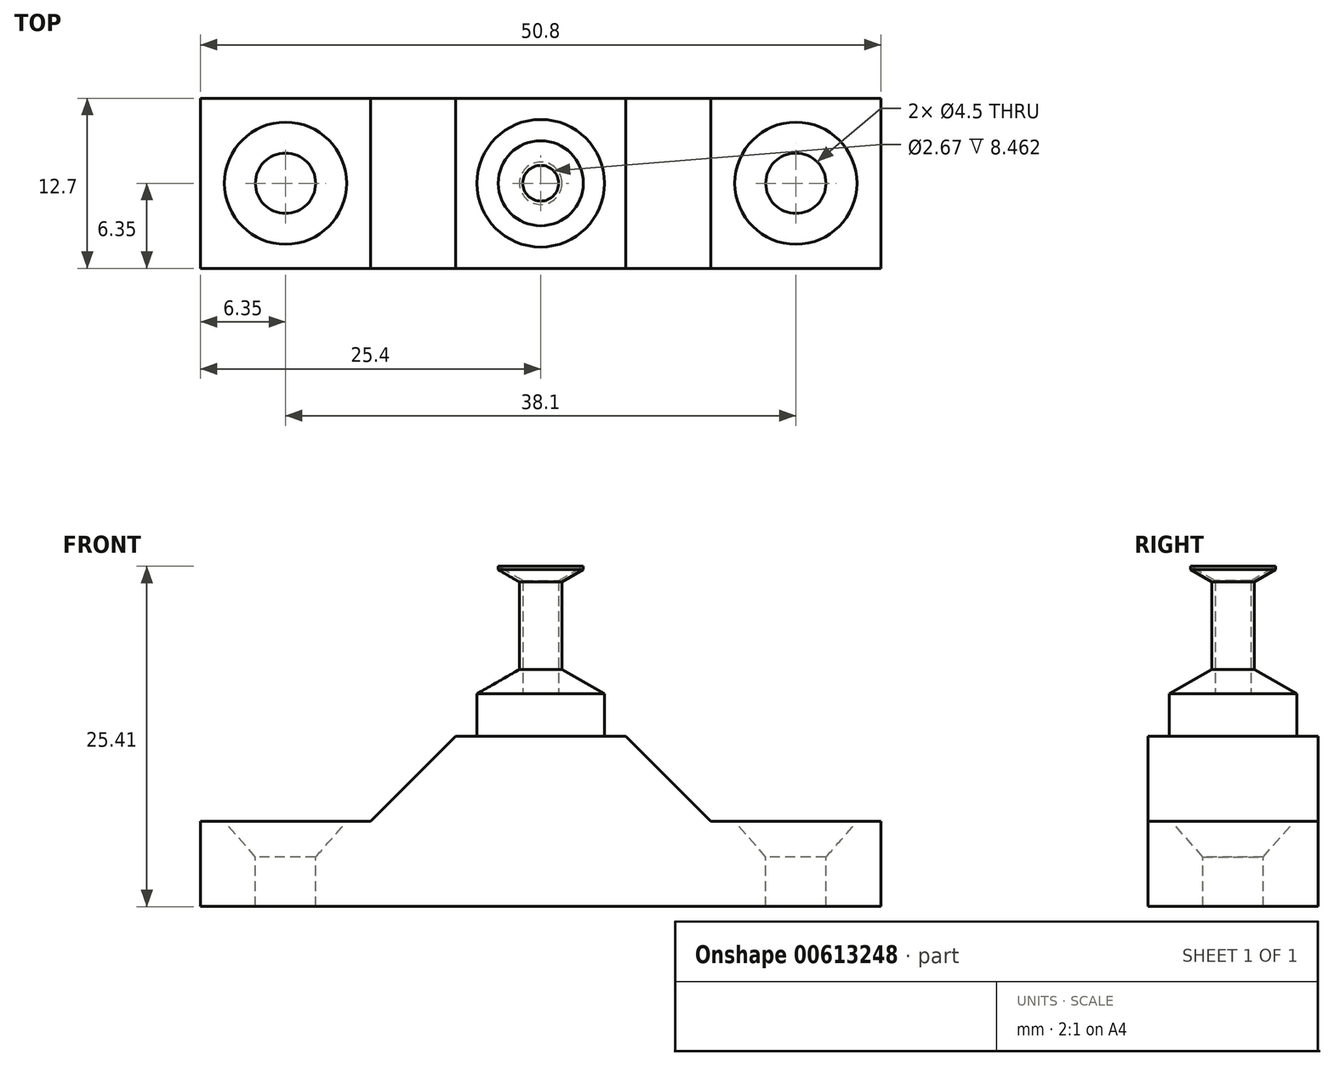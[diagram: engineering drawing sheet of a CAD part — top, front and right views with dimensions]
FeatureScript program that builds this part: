
annotation { "Feature Type Name" : "Feature", "Feature Type Description" : "" }
export const myFeature = defineFeature(function(context is Context, id is Id, definition is map)
    precondition{}
    {
        {
            var Q0;
            Q0=qCreatedBy(makeId("Front.planeOp"),FACE);
            var sketch = newSketch(context, id + "F0", { "sketchPlane" : qUnion([Q0])});
            skLineSegment(sketch, "E0.bottom", {"start": v(25.4, 3.18) * mm, "end": v(12.7, 3.18) * mm});
            skLineSegment(sketch, "E0.top", {"start": v(25.4, -3.18) * mm, "end": v(-25.4, -3.18) * mm});
            skLineSegment(sketch, "E0.left", {"start": v(25.4, 3.18) * mm, "end": v(25.4, -3.18) * mm});
            skLineSegment(sketch, "E0.right", {"start": v(-25.4, 3.18) * mm, "end": v(-25.4, -3.18) * mm});
            skPoint(sketch, "E0.middle", {"position": v(0, 0) * mm});
            skLineSegment(sketch, "E1", {"start": v(-12.7, 3.18) * mm, "end": v(-6.35, 9.53) * mm});
            skLineSegment(sketch, "E2", {"start": v(-6.35, 9.53) * mm, "end": v(6.35, 9.53) * mm});
            skLineSegment(sketch, "E3", {"start": v(6.35, 9.53) * mm, "end": v(12.7, 3.18) * mm});
            skLineSegment(sketch, "E4.trimOffspring", {"start": v(-12.7, 3.18) * mm, "end": v(-25.4, 3.18) * mm});
            skSolve(sketch);
        }
        {
            var Q0;
            Q0 = qSketchRegion(id + "F0", true);
            extrude(context, id + "F1", {"entities" : qUnion([Q0]), "endBound" : BoundingType.SYMMETRIC, "depth" : 12.7 * mm, "offsetDistance" : 25.4 * mm});
        }
        {
            var Q0;
            Q0=makeQuery(id+"F1.opExtrude","SWEPT_FACE",FACE,{"disambiguationData":[OSD([sQuery(id+"F0.wireOp",EDGE,"E4.trimOffspring")])]});
            var sketch = newSketch(context, id + "F2", { "sketchPlane" : qUnion([Q0])});
            skPoint(sketch, "E5", {"position": v(-19.05, 0) * mm});
            skPoint(sketch, "E6", {"position": v(19.05, 0) * mm});
            skSolve(sketch);
        }
        {
            var Q0;
            Q0=sQuery(id+"F2.wireOp",VERTEX,"E5");
            var Q1;
            Q1=sQuery(id+"F2.wireOp",VERTEX,"E6");
            var Q2;
            Q2=makeQuery(id+"F1.opExtrude","SWEPT_BODY",BODY,{"disambiguationData":[OSD([sQuery(id+"F0.wireOp",EDGE,"E0.bottom"),sQuery(id+"F0.wireOp",EDGE,"E0.top"),sQuery(id+"F0.wireOp",EDGE,"E0.left"),sQuery(id+"F0.wireOp",EDGE,"E0.right"),sQuery(id+"F0.wireOp",EDGE,"E1"),sQuery(id+"F0.wireOp",EDGE,"E2"),sQuery(id+"F0.wireOp",EDGE,"E3"),sQuery(id+"F0.wireOp",EDGE,"E4.trimOffspring")])]});
            hole(context, id + "F3", {"style" : HoleStyle.C_SINK, "endStyle" : HoleEndStyle.THROUGH, "standardTappedOrClearance" : lookupTablePath({ "standard" : "ANSI", "fit" : "Normal (ASME)", "size" : "#8", "type" : "Clearance" }), "standardBlindInLast" : lookupTablePath({ "fit" : "Free", "standard" : "ANSI", "size" : "#8", "type" : "Clearance" }), "holeDiameter" : 4.5 * mm, "cSinkDiameter" : 9.12 * mm, "cSinkAngle" : 82 * degree, "majorDiameter" : 6.35 * mm, "isTappedThrough" : true, "tappedDepth" : 12.7 * mm, "tapClearance" : 0, "startFromSketch" : true, "locations" : qUnion([Q0, Q1]), "scope" : qUnion([Q2])});
        }
        {
            var Q0;
            Q0=qCreatedBy(makeId("Front.planeOp"),FACE);
            var sketch = newSketch(context, id + "F4", { "sketchPlane" : qUnion([Q0])});
            skLineSegment(sketch, "E7", {"start": v(0, 9.53) * mm, "end": v(0, 12.7) * mm});
            skLineSegment(sketch, "E8", {"start": v(0, 12.7) * mm, "end": v(1.33, 12.7) * mm});
            skLineSegment(sketch, "E9", {"start": v(1.33, 12.7) * mm, "end": v(1.33, 21.16) * mm});
            skLineSegment(sketch, "E10", {"start": v(3.17, 22.23) * mm, "end": v(3.17, 21.97) * mm});
            skLineSegment(sketch, "E11", {"start": v(1.59, 21.05) * mm, "end": v(3.17, 21.97) * mm});
            skLineSegment(sketch, "E12", {"start": v(4.76, 12.7) * mm, "end": v(4.76, 9.53) * mm});
            skLineSegment(sketch, "E13", {"start": v(4.76, 9.53) * mm, "end": v(0, 9.53) * mm});
            skLineSegment(sketch, "E14", {"start": v(1.59, 21.05) * mm, "end": v(1.59, 14.53) * mm});
            skLineSegment(sketch, "E15", {"start": v(3.17, 22.23) * mm, "end": v(1.33, 21.16) * mm});
            skLineSegment(sketch, "E16", {"start": v(4.76, 12.7) * mm, "end": v(1.59, 14.53) * mm});
            skSolve(sketch);
        }
        {
            var Q0;
            Q0 = qSketchRegion(id + "F4", true);
            var Q1;
            Q1=sQuery(id+"F4.wireOp",EDGE,"E7");
            revolve(context, id + "F5", {"operationType" : NewBodyOperationType.ADD, "surfaceOperationType" : NewSurfaceOperationType.NEW, "entities" : qUnion([Q0]), "axis" : qUnion([Q1]), "revolveType" : RevolveType.FULL});
        }
    });
